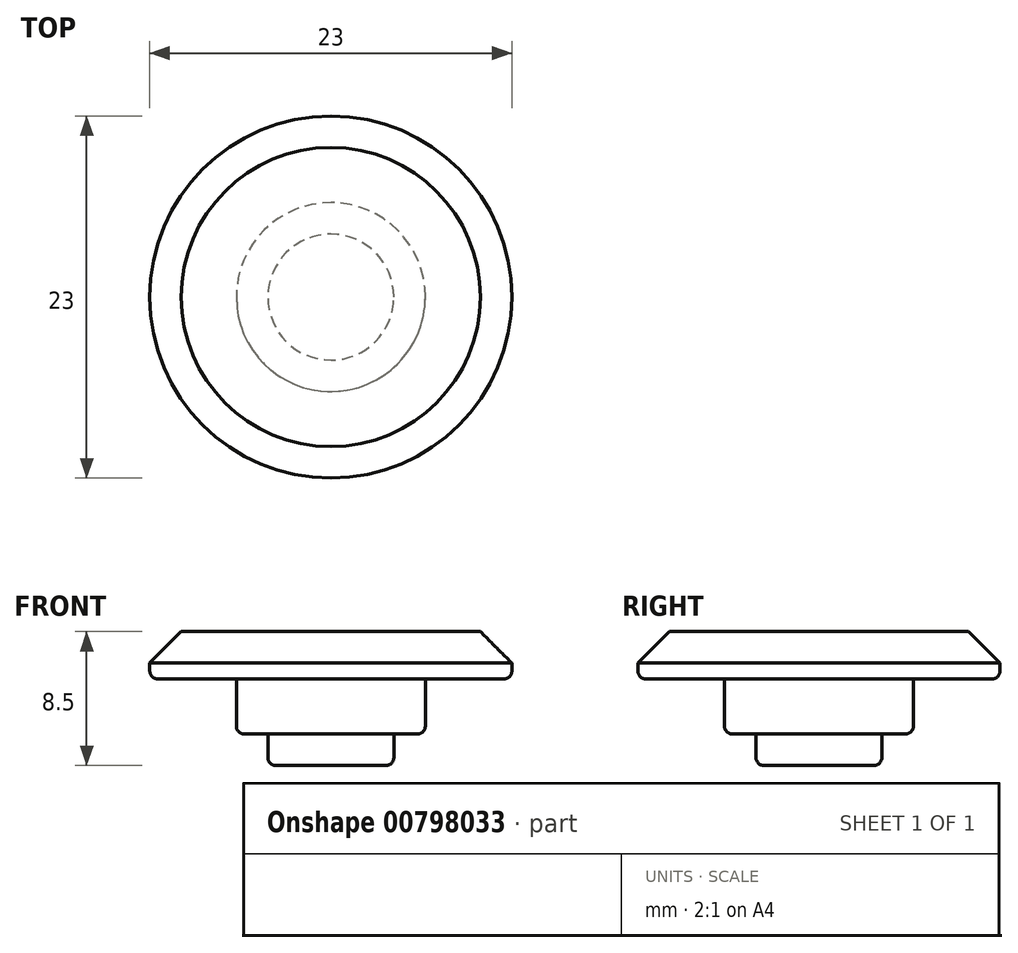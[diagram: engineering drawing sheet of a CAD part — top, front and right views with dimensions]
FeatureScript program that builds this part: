
annotation { "Feature Type Name" : "Feature", "Feature Type Description" : "" }
export const myFeature = defineFeature(function(context is Context, id is Id, definition is map)
    precondition{}
    {
        {
            var Q0;
            Q0=qCreatedBy(makeId("Top.planeOp"),FACE);
            var sketch = newSketch(context, id + "F0", { "sketchPlane" : qUnion([Q0])});
            skCircle(sketch, "E0", {"center": v(0, 0) * mm, "radius": 11.5 * mm});
            skSolve(sketch);
        }
        {
            var Q0;
            Q0 = qSketchRegion(id + "F0", true);
            extrude(context, id + "F1", {"entities" : qUnion([Q0]), "depth" : 3 * mm, "offsetDistance" : 25 * mm});
        }
        {
            var Q0;
            Q0=makeQuery(id+"F1.opExtrude","CAP_FACE",FACE,{"disambiguationData":[OSD([sQuery(id+"F0.wireOp",EDGE,"E0")])],"isStart":true});
            var sketch = newSketch(context, id + "F2", { "sketchPlane" : qUnion([Q0])});
            skCircle(sketch, "E1", {"center": v(0, 0) * mm, "radius": 4 * mm});
            skSolve(sketch);
        }
        {
            var Q0;
            Q0 = qSketchRegion(id + "F2", true);
            extrude(context, id + "F3", {"entities" : qUnion([Q0]), "operationType" : NewBodyOperationType.ADD, "depth" : 5.5 * mm, "offsetDistance" : 25 * mm});
        }
        {
            var Q0;
            Q0=makeQuery(id+"F1.opExtrude","CAP_FACE",FACE,{"disambiguationData":[OSD([sQuery(id+"F0.wireOp",EDGE,"E0")])],"isStart":true});
            var sketch = newSketch(context, id + "F4", { "sketchPlane" : qUnion([Q0])});
            skCircle(sketch, "E2", {"center": v(0, 0) * mm, "radius": 6 * mm});
            skSolve(sketch);
        }
        {
            var Q0;
            Q0 = qSketchRegion(id + "F4", true);
            extrude(context, id + "F5", {"entities" : qUnion([Q0]), "operationType" : NewBodyOperationType.ADD, "depth" : 3.5 * mm, "offsetDistance" : 25 * mm});
        }
        {
            var Q0;
            Q0=makeQuery(id+"F1.opExtrude","CAP_FACE",FACE,{"disambiguationData":[OSD([sQuery(id+"F0.wireOp",EDGE,"E0")])],"isStart":false});
            chamfer(context, id + "F6", {"entities" : qUnion([Q0]), "width" : 2 * mm, "tangentPropagation" : true});
        }
        {
            var Q0;
            Q0=makeQuery(id+"F5.opExtrude","CAP_EDGE",EDGE,{"disambiguationData":[OSD([sQuery(id+"F4.wireOp",EDGE,"E2")])],"isStart":false});
            var Q1;
            Q1=makeQuery(id+"F3.opExtrude","CAP_EDGE",EDGE,{"disambiguationData":[OSD([sQuery(id+"F2.wireOp",EDGE,"E1")])],"isStart":false});
            var Q2;
            Q2=makeQuery(id+"F1.opExtrude","CAP_EDGE",EDGE,{"disambiguationData":[OSD([sQuery(id+"F0.wireOp",EDGE,"E0")])],"isStart":true});
            fillet(context, id + "F7", {"entities" : qUnion([Q0, Q1, Q2]), "radius" : .5 * mm, "tangentPropagation" : true, "allowEdgeOverflow" : false});
        }
    });
